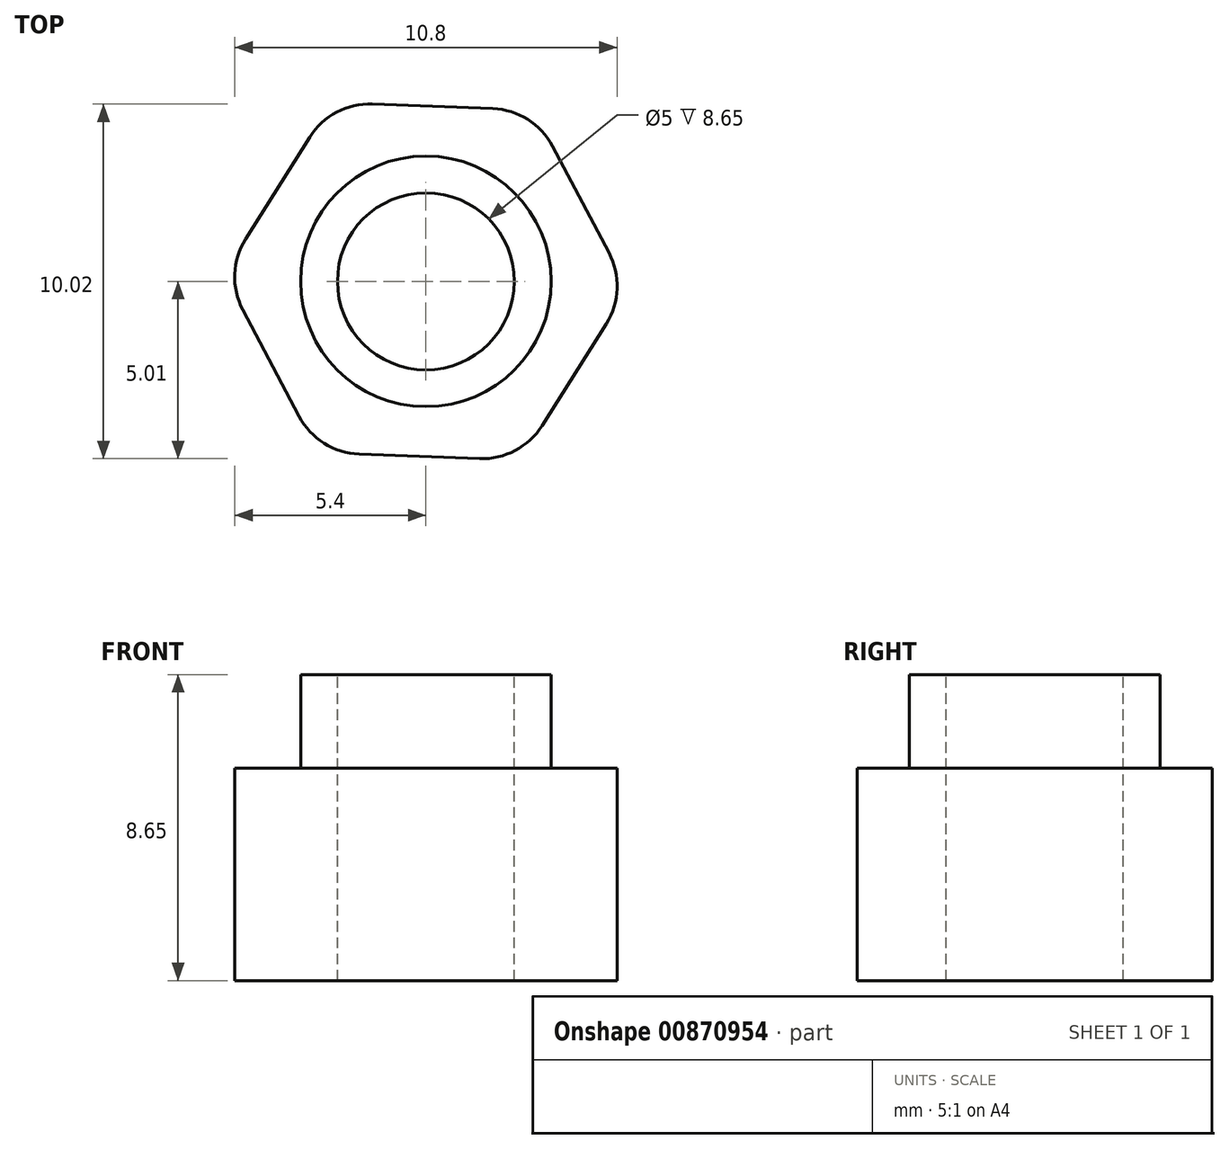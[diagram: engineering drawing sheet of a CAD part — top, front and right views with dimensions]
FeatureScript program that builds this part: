
annotation { "Feature Type Name" : "Feature", "Feature Type Description" : "" }
export const myFeature = defineFeature(function(context is Context, id is Id, definition is map)
    precondition{}
    {
        {
            var Q0;
            Q0=qCreatedBy(makeId("Top.planeOp"),FACE);
            var sketch = newSketch(context, id + "F0", { "sketchPlane" : qUnion([Q0])});
            skCircle(sketch, "E0.cCircle", {"center": v(0, 0) * mm, "radius": 4.95 * mm, "construction": true});
            skLineSegment(sketch, "E0.0", {"start": v(5.71, -0.22) * mm, "end": v(2.67, -5.05) * mm});
            skLineSegment(sketch, "E0.1", {"start": v(2.67, -5.05) * mm, "end": v(-3.04, -4.84) * mm});
            skLineSegment(sketch, "E0.2", {"start": v(-3.04, -4.84) * mm, "end": v(-5.71, 0.22) * mm});
            skLineSegment(sketch, "E0.3", {"start": v(-5.71, 0.22) * mm, "end": v(-2.67, 5.05) * mm});
            skLineSegment(sketch, "E0.4", {"start": v(-2.67, 5.05) * mm, "end": v(3.04, 4.84) * mm});
            skLineSegment(sketch, "E0.5", {"start": v(3.04, 4.84) * mm, "end": v(5.71, -0.22) * mm});
            skPoint(sketch, "E0.0.midPoint", {"position": v(4.2, -2.64) * mm});
            skSolve(sketch);
        }
        {
            var Q0;
            Q0=makeQuery(id+"F0.imprint","IMPRINT",FACE,{"disambiguationData":[TD([[makeQuery(id+"F0.imprint","IMPRINT",EDGE,{"derivedFrom":sQuery(id+"F0.wireOp",EDGE,"E0.0")}),-1.0]])]});
            extrude(context, id + "F1", {"entities" : qUnion([Q0]), "depth" : 6 * mm, "offsetDistance" : 25 * mm});
        }
        {
            var Q0;
            Q0=makeQuery(id+"F1.opExtrude","CAP_FACE",FACE,{"disambiguationData":[OSD([sQuery(id+"F0.wireOp",EDGE,"E0.0"),sQuery(id+"F0.wireOp",EDGE,"E0.1"),sQuery(id+"F0.wireOp",EDGE,"E0.2"),sQuery(id+"F0.wireOp",EDGE,"E0.3"),sQuery(id+"F0.wireOp",EDGE,"E0.4"),sQuery(id+"F0.wireOp",EDGE,"E0.5")])],"isStart":false});
            var sketch = newSketch(context, id + "F2", { "sketchPlane" : qUnion([Q0])});
            skCircle(sketch, "E1", {"center": v(0, 0) * mm, "radius": 3.54 * mm});
            skSolve(sketch);
        }
        {
            var Q0;
            Q0=makeQuery(id+"F2.imprint","IMPRINT",FACE,{"disambiguationData":[TD([[makeQuery(id+"F2.imprint","IMPRINT",EDGE,{"derivedFrom":sQuery(id+"F2.wireOp",EDGE,"E1")}),1.0]])]});
            extrude(context, id + "F3", {"entities" : qUnion([Q0]), "operationType" : NewBodyOperationType.ADD, "depth" : 2.65 * mm, "offsetDistance" : 25 * mm});
        }
        {
            var Q0;
            Q0=makeQuery(id+"F3.opExtrude","CAP_FACE",FACE,{"disambiguationData":[OSD([sQuery(id+"F2.wireOp",EDGE,"E1")])],"isStart":false});
            var sketch = newSketch(context, id + "F4", { "sketchPlane" : qUnion([Q0])});
            skCircle(sketch, "E2", {"center": v(0, 0) * mm, "radius": 2.5 * mm});
            skSolve(sketch);
        }
        {
            var Q0;
            Q0=makeQuery(id+"F4.imprint","IMPRINT",FACE,{"disambiguationData":[TD([[makeQuery(id+"F4.imprint","IMPRINT",EDGE,{"derivedFrom":sQuery(id+"F4.wireOp",EDGE,"E2")}),1.0]])]});
            extrude(context, id + "F5", {"entities" : qUnion([Q0]), "operationType" : NewBodyOperationType.REMOVE, "oppositeDirection" : true, "depth" : 25 * mm, "offsetDistance" : 25 * mm});
        }
        {
            var Q0;
            Q0=makeQuery(id+"F1.opExtrude","SWEPT_EDGE",EDGE,{"disambiguationData":[OSD([sQuery(id+"F0.wireOp",EDGE,"E0.0"),sQuery(id+"F0.wireOp",EDGE,"E0.1")])]});
            var Q1;
            Q1=makeQuery(id+"F1.opExtrude","SWEPT_EDGE",EDGE,{"disambiguationData":[OSD([sQuery(id+"F0.wireOp",EDGE,"E0.0"),sQuery(id+"F0.wireOp",EDGE,"E0.5")])]});
            var Q2;
            Q2=makeQuery(id+"F1.opExtrude","SWEPT_EDGE",EDGE,{"disambiguationData":[OSD([sQuery(id+"F0.wireOp",EDGE,"E0.1"),sQuery(id+"F0.wireOp",EDGE,"E0.2")])]});
            var Q3;
            Q3=makeQuery(id+"F1.opExtrude","SWEPT_EDGE",EDGE,{"disambiguationData":[OSD([sQuery(id+"F0.wireOp",EDGE,"E0.2"),sQuery(id+"F0.wireOp",EDGE,"E0.3")])]});
            var Q4;
            Q4=makeQuery(id+"F1.opExtrude","SWEPT_EDGE",EDGE,{"disambiguationData":[OSD([sQuery(id+"F0.wireOp",EDGE,"E0.3"),sQuery(id+"F0.wireOp",EDGE,"E0.4")])]});
            var Q5;
            Q5=makeQuery(id+"F1.opExtrude","SWEPT_EDGE",EDGE,{"disambiguationData":[OSD([sQuery(id+"F0.wireOp",EDGE,"E0.4"),sQuery(id+"F0.wireOp",EDGE,"E0.5")])]});
            fillet(context, id + "F6", {"entities" : qUnion([Q0, Q1, Q2, Q3, Q4, Q5]), "radius" : 2 * mm, "tangentPropagation" : true, "allowEdgeOverflow" : false});
        }
    });
